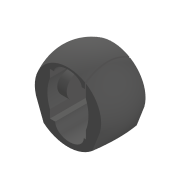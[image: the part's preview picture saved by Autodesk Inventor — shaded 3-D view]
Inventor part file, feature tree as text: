
AUTODESK INVENTOR PART (.ipt)
format: ipt  version: 2020 (Build 240168000, 168)  size: 803,840 bytes
history: native  units: mm
features: sketch x6, plane x3, extrude x3, other x2, loft x1, projected_geometry x1
ambient origin geometry x8: Origin, YZ Plane, XZ Plane, XY Plane, X Axis, Y Axis, Z Axis, Center Point
bodies: Solid1 (feature_tree)
feature tree (16):
  sketch  "Sketch1"  dims[d16=4.5mm d17=4.5mm]
  plane  "Work Plane1"
  sketch  "Sketch2"  dims[d19=0.0mm d20=90.0deg d21=0.0mm d22=90.0deg]
  plane  "Work Plane2"
  loft  "Loft1"
  extrude  "Extrusion1"  TaperAngle=0.0deg  [1 undecoded]
  plane  "Work Plane3"
  extrude  "Extrusion2"  Depth=0.2mm
  extrude  "Extrusion3"  Depth=10.0mm
  other  "Image1"
  sketch  "Sketch3"  dims[d23=0.0mm d24=90.0deg d32=0.2mm]
  sketch  "Sketch4"  dims[d34=10.0mm d35=0.0mm d36=5.0mm]
  other  "Image2"
  sketch  "Sketch5"  dims[d37=10.0mm d38=0.0mm]
  projected_geometry  "Projected Loop1"
  sketch  "Sketch6"  dims[d39=4.5mm d40=0.0mm d33=0.5mm]
note: 1 required parameter value undecoded (feature->parameter linkage not recoverable at this tier; creation-order binding heuristic only, values carry confidence <= 0.55)
